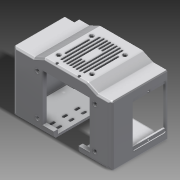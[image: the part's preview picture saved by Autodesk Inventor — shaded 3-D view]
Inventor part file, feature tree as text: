
AUTODESK INVENTOR PART (.ipt)
format: ipt  version: 2015 (Build 190159000, 159)  size: 862,720 bytes
history: native  units: in
note: dims shown in document units (in); Inventor stores cm internally (conversion verified against a paired STEP export)
features: reference x16, extrude x15, sketch x12, chamfer x9, fillet x7, projected_geometry x4, plane x1, other x1
ambient origin geometry x8: Origin, YZ Plane, XZ Plane, XY Plane, X Axis, Y Axis, Z Axis, Center Point
bodies: Body1 (feature_tree)
feature tree (65):
  plane  "Work Plane1"
  extrude  "Extrusion3"  Depth=0.1181in TaperAngle=0.0deg
  extrude  "Extrusion4"  Depth=0.9843in
  extrude  "Extrusion9"  Depth=2.3622in TaperAngle=0.0deg
  extrude  "Extrusion5"  Depth=0.0787in
  extrude  "Extrusion6"  Depth=0.0787in
  chamfer  "Chamfer1"  Distance=0.0394in
  chamfer  "Chamfer2"  Distance=0.2362in
  chamfer  "Chamfer5"  Distance=0.0787in
  chamfer  "Chamfer7"  Distance=1.0651in
  chamfer  "Chamfer8"  Distance=0.5118in
  chamfer  "Chamfer9"  Distance=1.9685in
  chamfer  "Chamfer10"  Distance=1.0651in
  fillet  "Fillet5"  Radius=0.5118in
  fillet  "Fillet6"  Radius=0.1181in
  fillet  "Fillet14"  Radius=0.1181in
  extrude  "Extrusion7"  Depth=0.1181in
  other  "Lip1"
  extrude  "Extrusion15"  Depth=0.1181in
  extrude  "Extrusion8"  Depth=0.2362in TaperAngle=0.0deg
  chamfer  "Chamfer4"  Distance=0.0787in
  fillet  "Fillet11"  Radius=0.0394in
  fillet  "Fillet12"  Radius=0.0787in
  extrude  "Extrusion10"  Depth=0.2362in
  extrude  "Extrusion11"  Depth=0.2362in
  extrude  "Extrusion12"  Depth=0.3937in TaperAngle=0.0deg
  fillet  "Fillet13"  Radius=1.189in
  chamfer  "Chamfer6"  Distance=0.3937in
  extrude  "Extrusion13"  Depth=0.2362in
  fillet  "Fillet15"  Radius=0.1969in
  extrude  "Extrusion14"  Depth=0.3937in
  extrude  "Extrusion16"  Depth=0.2362in
  extrude  "Extrusion17"  Depth=0.2362in
  sketch  "Sketch4"  dims[d10=0.1969in d11=0.0in d12=0.1181in d13=2.4803in d14=0.0in]
  projected_geometry  "Projected Loop2"
  sketch  "Sketch5"  dims[d17=2.7724in d18=0.0in d19=0.9843in]
  sketch  "Sketch6"  dims[d20=0.5118in d25=2.3622in d26=0.0in]
  reference  "Reference18"
  reference  "Reference19"
  reference  "Reference21"
  sketch  "Sketch7"  dims[d31=0.1575in d32=0.0787in d33=0.1374in d34=0.1575in d35=0.0787in d36=0.1374in]
  reference  "Reference23"
  reference  "Reference24"
  reference  "Reference25"
  reference  "Reference26"
  reference  "Reference28"
  reference  "Reference31"
  reference  "Reference32"
  reference  "Reference33"
  reference  "Reference34"
  reference  "Reference35"
  reference  "Reference36"
  reference  "Reference37"
  reference  "Reference38"
  sketch  "Sketch9"  dims[d40=0.0787in d41=0.0787in]
  projected_geometry  "Projected Loop3"
  projected_geometry  "Projected Loop4"
  sketch  "Sketch10"  dims[d46=0.0787in d47=0.0394in d48=0.0in]
  projected_geometry  "Projected Loop5"
  sketch  "Sketch11"  dims[d49=0.0394in d50=0.0394in d51=0.0in d52=0.0in d53=0.0in d54=0.0in]
  sketch  "Sketch14"  dims[d55=0.1181in]
  sketch  "Sketch15"  dims[d58=0.1181in d59=0.2362in d60=0.0in d61=0.0472in d62=0.0787in d63=0.1374in]
  sketch  "Sketch16"  dims[d65=1.5748in]
  sketch  "Sketch17"  dims[d66=2.1654in]
  sketch  "Sketch18"  dims[d70=0.1181in d71=1.0651in d72=0.5118in d73=1.9685in d74=1.0651in d75=0.5118in d76=0.1181in d77=0.1181in d78=0.1181in d79=0.1181in d80=0.2362in d81=0.0in d82=0.1575in d83=0.0787in d84=0.1374in d85=0.0394in d86=0.0787in d87=1.9685in d88=1.9685in d101=0.3937in d102=0.0in d104=1.189in d106=0.3937in d107=0.0in d108=0.1378in d109=0.1969in d110=0.7874in d112=1.5748in d113=0.3937in d115=0.3937in d117=1.5748in d118=1.5855in d119=0.3543in d121=1.1811in d123=0.0787in d124=0.0394in d125=0.0984in d131=0.0787in d132=1.8898in d133=0.0787in d134=0.0394in d135=0.0787in d136=1.9685in d137=0.0787in d138=0.0394in d147=0.0787in d148=0.5906in d151=0.0394in d152=0.0787in d153=1.9685in d154=0.0787in d155=0.0394in d156=0.0787in d157=0.0394in d158=0.7874in d160=1.378in d161=0.3937in d163=0.3937in d165=0.7874in d167=0.6102in d168=0.3937in d170=0.3937in d172=0.374in d175=1.0827in d180=0.0787in d181=0.7874in d183=1.3976in d184=0.3937in d186=0.3937in d188=0.0787in d189=0.315in d190=0.0in d191=0.1969in d193=0.0394in d194=0.0787in d195=45.0deg d196=0.5512in d197=1.0323in d198=0.315in d199=1.4327in d200=2.2579in d201=2.2579in d204=0.1181in d205=0.1181in d206=0.1181in d207=0.1575in d208=0.0787in d209=45.0deg d210=0.1575in d211=0.0787in d212=45.0deg d213=0.1575in d214=0.0787in d215=30.0deg d216=0.0787in d217=0.0787in d218=0.0787in d219=45.0deg d220=0.3543in d221=0.3543in d222=0.3543in d223=0.315in d224=0.1575in d225=0.0787in d226=0.0in d227=0.0394in d228=0.1181in d229=0.1969in d230=0.3937in d231=2.0472in d232=0.0394in d233=0.3937in d234=0.1969in d235=0.1181in d236=2.0472in d237=0.0394in d238=0.1969in d239=0.0in d240=0.0787in d241=0.3543in d242=0.4374in d243=0.1575in d244=0.1575in d245=0.3937in d246=0.0in d247=0.0787in d248=0.0787in d249=4.7228in d250=4.4866in d259=0.15in d260=0.2362in d261=0.2362in d262=0.15in d263=1.5602in d264=1.2465in d265=2.8854in d266=1.7362in d267=1.1811in d269=0.5906in d270=0.3937in d272=0.3937in d274=0.7874in d276=0.315in d277=0.3937in d279=0.3937in d281=0.7874in d283=0.315in d284=0.3937in d286=0.3937in d288=0.1181in d289=0.1181in d290=1.063in d291=0.105in d292=0.105in d293=90.0deg d294=0.7874in d295=0.0in d296=0.5109in d297=0.0394in d298=0.0394in d299=0.0394in d300=0.2362in d301=0.0in]
